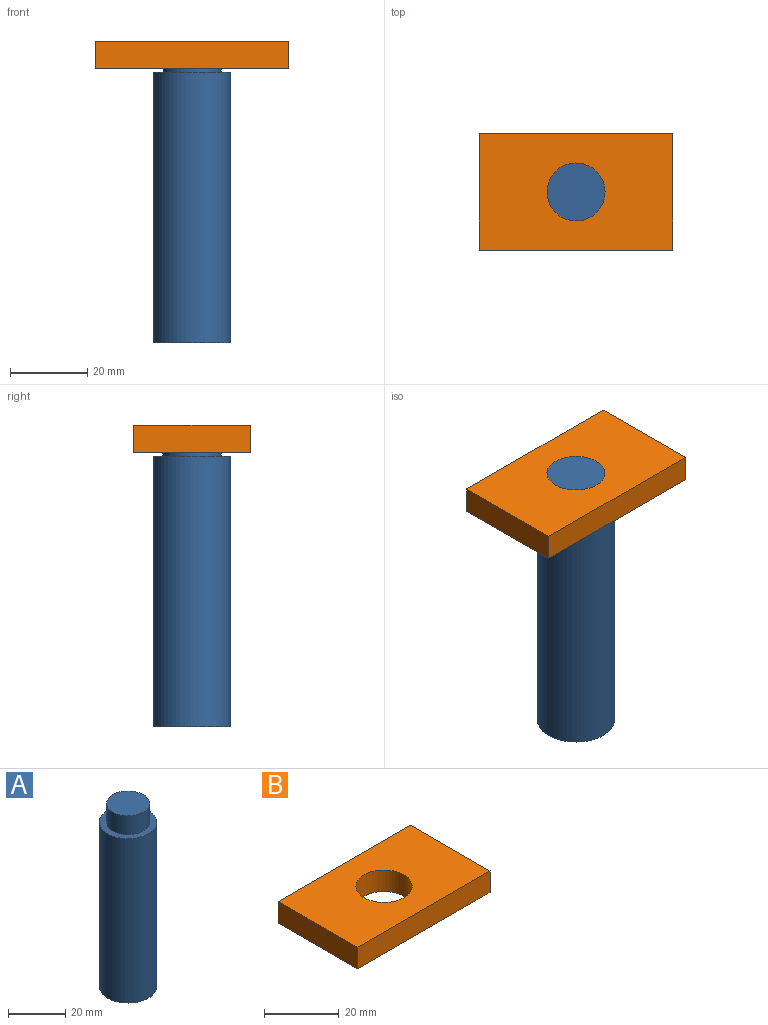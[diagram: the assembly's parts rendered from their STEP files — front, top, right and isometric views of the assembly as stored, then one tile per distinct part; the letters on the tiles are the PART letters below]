
ASSEMBLY  parts=2 mates=1
PART A: 5 faces, bbox 20x20x78 mm
  f0: cylinder r=10mm len=70mm, axis (0,0,-1), area 4398.2mm2, adj f1,f2
  f1: plane 20x20mm, normal (0,0,1), area 137.4mm2, adj f0,f3
  f2: plane 20x20mm, normal (0,0,-1), area 314.2mm2, adj f0
  f3: cylinder r=7.5mm len=15mm, axis (0,0,-1), area 377mm2, adj f1,f4
  f4: plane 15x15mm, normal (0,0,1), area 176.7mm2, adj f3
PART B: 7 faces, bbox 50x30x7 mm
  f0: plane 50x7mm, normal (0,-1,0), area 350mm2, adj f1,f4,f5,f6
  f1: plane 30x7mm, normal (1,0,0), area 210mm2, adj f0,f2,f5,f6
  f2: plane 50x7mm, normal (0,1,0), area 350mm2, adj f1,f4,f5,f6
  f3: cylinder r=7.5mm len=15mm, axis (0,0,-1), area 329.9mm2, adj f5,f6
  f4: plane 30x7mm, normal (-1,0,0), area 210mm2, adj f0,f2,f5,f6
  f5: plane 50x30mm, normal (0,0,1), area 1323.3mm2, adj f0,f1,f2,f3,f4
  f6: plane 50x30mm, normal (0,0,-1), area 1323.3mm2, adj f0,f1,f2,f3,f4
PLACE A t=(-43.66,6.83,22.21)mm
PLACE B t=(-43.66,6.83,93.21)mm
MATE revolute B.f3 <-> A.f3  axis (0,0,1) through (-43.66,6.83,100.21)mm
